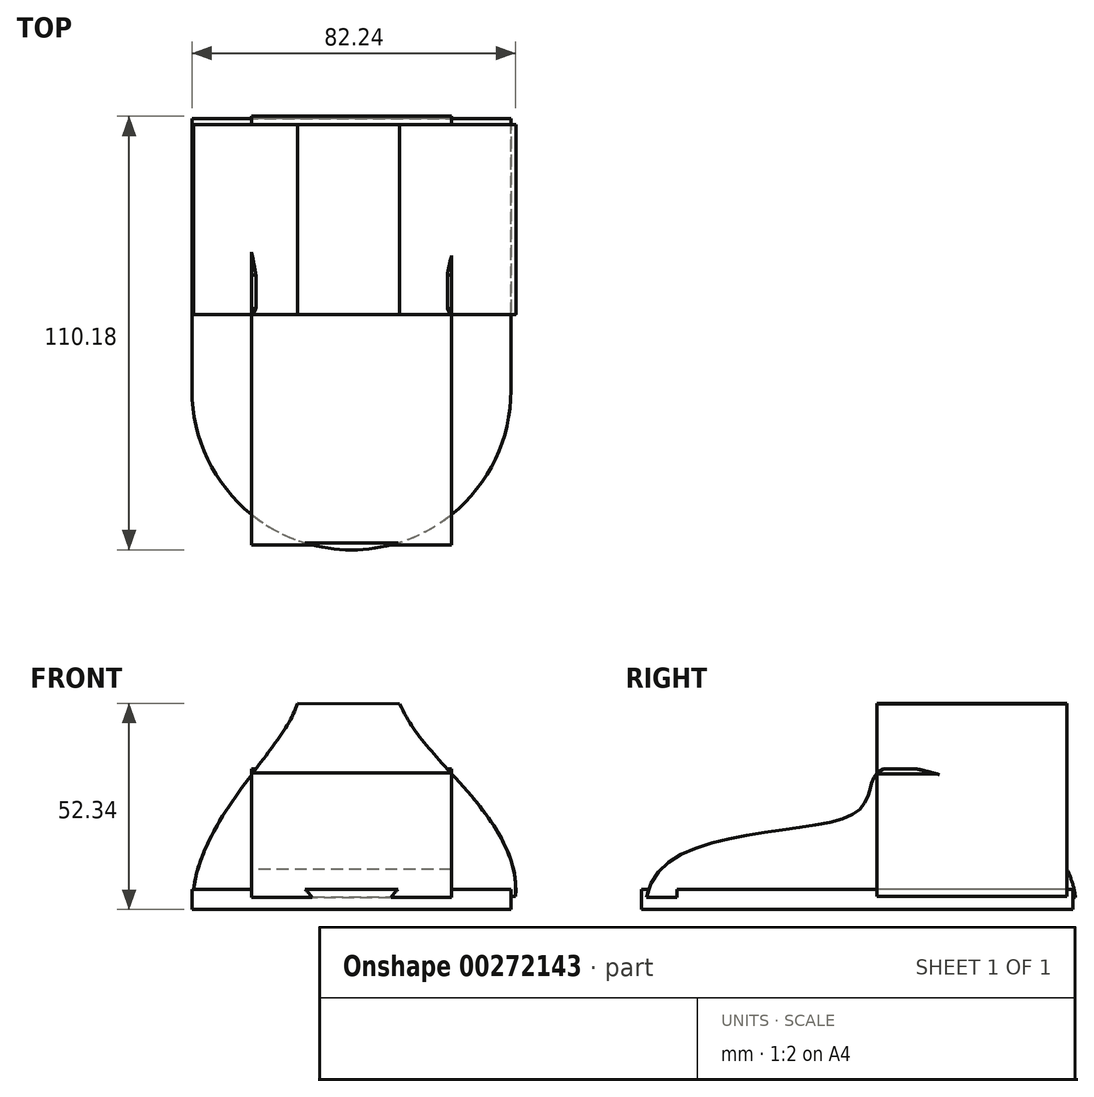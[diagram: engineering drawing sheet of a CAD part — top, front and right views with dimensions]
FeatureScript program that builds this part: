
annotation { "Feature Type Name" : "Feature", "Feature Type Description" : "" }
export const myFeature = defineFeature(function(context is Context, id is Id, definition is map)
    precondition{}
    {
        {
            var Q0;
            Q0=qCreatedBy(makeId("Top.planeOp"),FACE);
            var sketch = newSketch(context, id + "F0", { "sketchPlane" : qUnion([Q0])});
            skLineSegment(sketch, "E0.bottom", {"start": v(-40.52, 34.54) * mm, "end": v(40.52, 34.54) * mm});
            skLineSegment(sketch, "E0.top", {"start": v(-40.52, -34.54) * mm, "end": v(40.52, -34.54) * mm});
            skLineSegment(sketch, "E0.left", {"start": v(-40.52, 34.54) * mm, "end": v(-40.52, -34.54) * mm});
            skLineSegment(sketch, "E0.right", {"start": v(40.52, 34.54) * mm, "end": v(40.52, -34.54) * mm});
            skPoint(sketch, "E0.middle", {"position": v(0, 0) * mm});
            skCircle(sketch, "E1", {"center": v(0, -34.54) * mm, "radius": 40.52 * mm});
            skSolve(sketch);
        }
        {
            var Q0;
            Q0=makeQuery(id+"F0.imprint","IMPRINT",FACE,{"disambiguationData":[TD([[makeQuery(id+"F0.imprint","IMPRINT",EDGE,{"derivedFrom":sQuery(id+"F0.wireOp",EDGE,"E0.bottom")}),-1.0]])]});
            var Q1;
            {var subQ0=sQuery(id+"F0.wireOp",EDGE,"E0.top");Q1=makeQuery(id+"F0.imprint","IMPRINT",FACE,{"disambiguationData":[TD([[makeQuery(id+"F0.imprint","IMPRINT",EDGE,{"derivedFrom":subQ0}),-1.0]])]});}
            var Q2;
            {var subQ0=sQuery(id+"F0.wireOp",EDGE,"E0.top");Q2=makeQuery(id+"F0.imprint","IMPRINT",FACE,{"disambiguationData":[TD([[makeQuery(id+"F0.imprint","IMPRINT",EDGE,{"derivedFrom":subQ0}),1.0]])]});}
            extrude(context, id + "F1", {"entities" : qUnion([Q0, Q1, Q2]), "depth" : 5.08 * mm});
        }
        {
            var Q0;
            Q0=qCreatedBy(makeId("Right.planeOp"),FACE);
            var sketch = newSketch(context, id + "F2", { "sketchPlane" : qUnion([Q0])});
            skFitSpline(sketch, "E2", {"points": [v(-73.97, 0) * mm, v(-20.73, 24.55) * mm, v(-13.7, 35.64) * mm, v(35.13, 0) * mm], "startDerivative": vector(-5.43, 170.17) * mm, "endDerivative": vector(-13.87, -169.43) * mm});
            skLineSegment(sketch, "E3", {"start": v(-13.7, 35.64) * mm, "end": v(21.3, 35.64) * mm});
            skFitSpline(sketch, "E4", {"points": [v(21.3, 35.64) * mm, v(35.13, 3.07) * mm], "startDerivative": vector(0.88, -35.6) * mm, "endDerivative": vector(3.02, -32) * mm});
            skLineSegment(sketch, "E5", {"start": v(35.13, 3.07) * mm, "end": v(-73.78, 3.07) * mm});
            skSolve(sketch);
        }
        {
            var Q0;
            {var subQ0=sQuery(id+"F2.wireOp",EDGE,"E5");Q0=makeQuery(id+"F2.imprint","IMPRINT",FACE,{"disambiguationData":[TD([[makeQuery(id+"F2.imprint","IMPRINT",EDGE,{"derivedFrom":subQ0}),-1.0]])]});}
            var Q1;
            {var subQ0=sQuery(id+"F2.wireOp",EDGE,"E3");var subQ1=sQuery(id+"F2.wireOp",EDGE,"E2");var subQ2=makeQuery(id+"F2.imprint","INTERSECT",VERTEX,{"disambiguationData":[OD(1.0)],"derivedFrom":[subQ1,subQ0]});Q1=makeQuery(id+"F2.imprint","IMPRINT",FACE,{"disambiguationData":[TD([[makeQuery(id+"F2.imprint","IMPRINT",EDGE,{"disambiguationData":[TD([[subQ2,-1.0]])],"derivedFrom":subQ1}),1.0]])]});}
            extrude(context, id + "F3", {"entities" : qUnion([Q0, Q1]), "operationType" : NewBodyOperationType.ADD, "endBound" : BoundingType.SYMMETRIC, "depth" : 50.8 * mm});
        }
        {
            var Q0;
            Q0=qCreatedBy(makeId("Front.planeOp"),FACE);
            var sketch = newSketch(context, id + "F4", { "sketchPlane" : qUnion([Q0])});
            skFitSpline(sketch, "E6", {"points": [v(-40.22, 4.52) * mm, v(-24.48, 35.41) * mm, v(-13.71, 52.34) * mm], "startDerivative": vector(7.02, 60.7) * mm, "endDerivative": vector(10.8, 34.11) * mm});
            skFitSpline(sketch, "E7", {"points": [v(41.64, 3.28) * mm, v(24.4, 35.55) * mm, v(12.24, 52.13) * mm], "startDerivative": vector(6, 65.81) * mm, "endDerivative": vector(-20.46, 43.39) * mm});
            skLineSegment(sketch, "E8", {"start": v(-13.71, 52.34) * mm, "end": v(12.24, 52.13) * mm});
            skLineSegment(sketch, "E9", {"start": v(-40.22, 4.52) * mm, "end": v(41.64, 3.28) * mm});
            skSolve(sketch);
        }
        {
            var Q0;
            Q0=makeQuery(id+"F4.imprint","IMPRINT",FACE,{"disambiguationData":[TD([[makeQuery(id+"F4.imprint","IMPRINT",EDGE,{"derivedFrom":sQuery(id+"F4.wireOp",EDGE,"E6")}),-1.0]])]});
            extrude(context, id + "F5", {"entities" : qUnion([Q0]), "operationType" : NewBodyOperationType.ADD, "oppositeDirection" : true, "depth" : 33.02 * mm});
        }
        {
            var Q0;
            {var subQ0=sQuery(id+"F4.wireOp",EDGE,"E6");Q0=makeQuery(id+"F5.boolean.opBoolean","SPLIT",FACE,{"disambiguationData":[TD([makeQuery(id+"F3.opExtrude","CAP_FACE",FACE,{"disambiguationData":[OSD([sQuery(id+"F2.wireOp",EDGE,"E2"),sQuery(id+"F2.wireOp",EDGE,"E3"),sQuery(id+"F2.wireOp",EDGE,"E4"),sQuery(id+"F2.wireOp",EDGE,"E5")])],"isStart":true})])],"derivedFrom":makeQuery(id+"F5.opExtrude","CAP_FACE",FACE,{"disambiguationData":[OSD([subQ0,sQuery(id+"F4.wireOp",EDGE,"E7"),sQuery(id+"F4.wireOp",EDGE,"E8"),sQuery(id+"F4.wireOp",EDGE,"E9")])],"isStart":true})});}
            var Q1;
            {var subQ0=sQuery(id+"F4.wireOp",EDGE,"E6");var subQ1=sQuery(id+"F4.wireOp",EDGE,"E8");var subQ2=sQuery(id+"F4.wireOp",EDGE,"E7");Q1=makeQuery(id+"F5.boolean.opBoolean","SPLIT",FACE,{"disambiguationData":[TD([makeQuery(id+"F3.opExtrude","SWEPT_FACE",FACE,{"disambiguationData":[OSD([sQuery(id+"F2.wireOp",EDGE,"E3")])]})])],"derivedFrom":makeQuery(id+"F5.opExtrude","CAP_FACE",FACE,{"disambiguationData":[OSD([subQ0,subQ2,subQ1,sQuery(id+"F4.wireOp",EDGE,"E9")])],"isStart":true})});}
            var Q2;
            {var subQ0=sQuery(id+"F4.wireOp",EDGE,"E7");var subQ1=sQuery(id+"F0.wireOp",EDGE,"E0.right");var subQ2=sQuery(id+"F4.wireOp",EDGE,"E9");Q2=makeQuery(id+"F5.boolean.opBoolean","SPLIT",FACE,{"disambiguationData":[TD([makeQuery(id+"F1.opExtrude","SWEPT_FACE",FACE,{"disambiguationData":[OSD([subQ1])]})])],"derivedFrom":makeQuery(id+"F5.opExtrude","CAP_FACE",FACE,{"disambiguationData":[OSD([sQuery(id+"F4.wireOp",EDGE,"E6"),subQ0,sQuery(id+"F4.wireOp",EDGE,"E8"),subQ2])],"isStart":true})});}
            extrude(context, id + "F6", {"entities" : qUnion([Q0, Q1, Q2]), "operationType" : NewBodyOperationType.ADD, "depth" : 15.24 * mm});
        }
    });
